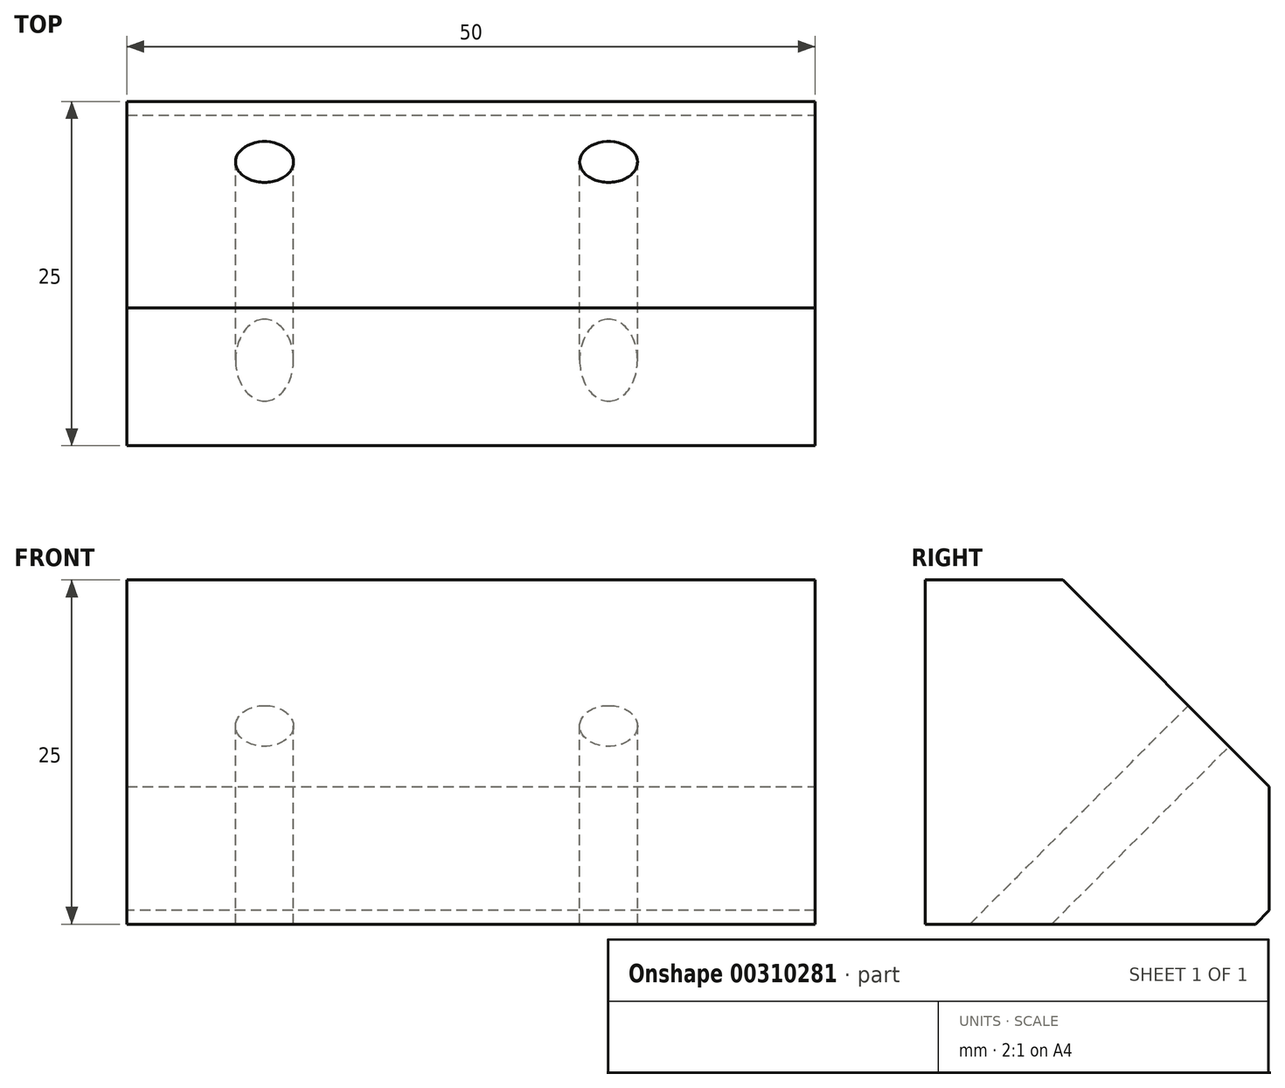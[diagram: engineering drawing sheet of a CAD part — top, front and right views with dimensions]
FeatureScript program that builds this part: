
annotation { "Feature Type Name" : "Feature", "Feature Type Description" : "" }
export const myFeature = defineFeature(function(context is Context, id is Id, definition is map)
    precondition{}
    {
        {
            var Q0;
            Q0=qCreatedBy(makeId("Top.planeOp"),FACE);
            var sketch = newSketch(context, id + "F0", { "sketchPlane" : qUnion([Q0])});
            skLineSegment(sketch, "E0.bottom", {"start": v(0, 25) * mm, "end": v(50, 25) * mm});
            skLineSegment(sketch, "E0.top", {"start": v(0, 0) * mm, "end": v(50, 0) * mm});
            skLineSegment(sketch, "E0.left", {"start": v(0, 25) * mm, "end": v(0, 0) * mm});
            skLineSegment(sketch, "E0.right", {"start": v(50, 25) * mm, "end": v(50, 0) * mm});
            skSolve(sketch);
        }
        {
            var Q0;
            Q0=makeQuery(id+"F0.imprint","IMPRINT",FACE,{"disambiguationData":[TD([[makeQuery(id+"F0.imprint","IMPRINT",EDGE,{"derivedFrom":sQuery(id+"F0.wireOp",EDGE,"E0.bottom")}),-1.0]])]});
            extrude(context, id + "F1", {"entities" : qUnion([Q0]), "depth" : 25 * mm});
        }
        {
            var Q0;
            Q0=makeQuery(id+"F1.opExtrude","CAP_EDGE",EDGE,{"disambiguationData":[OSD([sQuery(id+"F0.wireOp",EDGE,"E0.bottom")])],"isStart":false});
            chamfer(context, id + "F2", {"entities" : qUnion([Q0]), "width" : 15 * mm, "tangentPropagation" : true});
        }
        {
            var Q0;
            Q0=makeQuery(id+"F2.opChamfer","BLEND_FACE",FACE,{"disambiguationData":[OSD([sQuery(id+"F0.wireOp",EDGE,"E0.bottom")])]});
            var sketch = newSketch(context, id + "F3", { "sketchPlane" : qUnion([Q0])});
            skPoint(sketch, "E1", {"position": v(-10, -4.4) * mm});
            skPoint(sketch, "E2", {"position": v(-35, -4.4) * mm});
            skPoint(sketch, "E3", {"position": v(0, 0) * mm});
            skSolve(sketch);
        }
        {
            var Q0;
            Q0=sQuery(id+"F3.wireOp",VERTEX,"E1");
            var Q1;
            Q1=sQuery(id+"F3.wireOp",VERTEX,"E2");
            var Q2;
            Q2=makeQuery(id+"F1.opExtrude","SWEPT_BODY",BODY,{"disambiguationData":[OSD([sQuery(id+"F0.wireOp",EDGE,"E0.bottom"),sQuery(id+"F0.wireOp",EDGE,"E0.top"),sQuery(id+"F0.wireOp",EDGE,"E0.left"),sQuery(id+"F0.wireOp",EDGE,"E0.right")])]});
            hole(context, id + "F4", {"style" : HoleStyle.SIMPLE, "endStyle" : HoleEndStyle.THROUGH, "standardTappedOrClearance" : lookupTablePath({ "standard" : "ISO", "engagement" : "75%", "pitch" : "0.8 mm", "size" : "M5", "type" : "Tapped" }), "standardBlindInLast" : lookupTablePath({ "standard" : "ISO", "engagement" : "75%", "pitch" : "0.8 mm", "size" : "M5", "type" : "Tapped" }), "holeDiameter" : 4.2 * mm, "showTappedDepth" : true, "tappedDepth" : 12 * mm, "tapClearance" : 3, "locations" : qUnion([Q0, Q1]), "scope" : qUnion([Q2]), "majorDiameter" : 5 * mm});
        }
        {
            var Q0;
            Q0=makeQuery(id+"F1.opExtrude","CAP_EDGE",EDGE,{"disambiguationData":[OSD([sQuery(id+"F0.wireOp",EDGE,"E0.bottom")])],"isStart":true});
            chamfer(context, id + "F5", {"entities" : qUnion([Q0]), "width" : 1 * mm, "tangentPropagation" : true});
        }
    });
